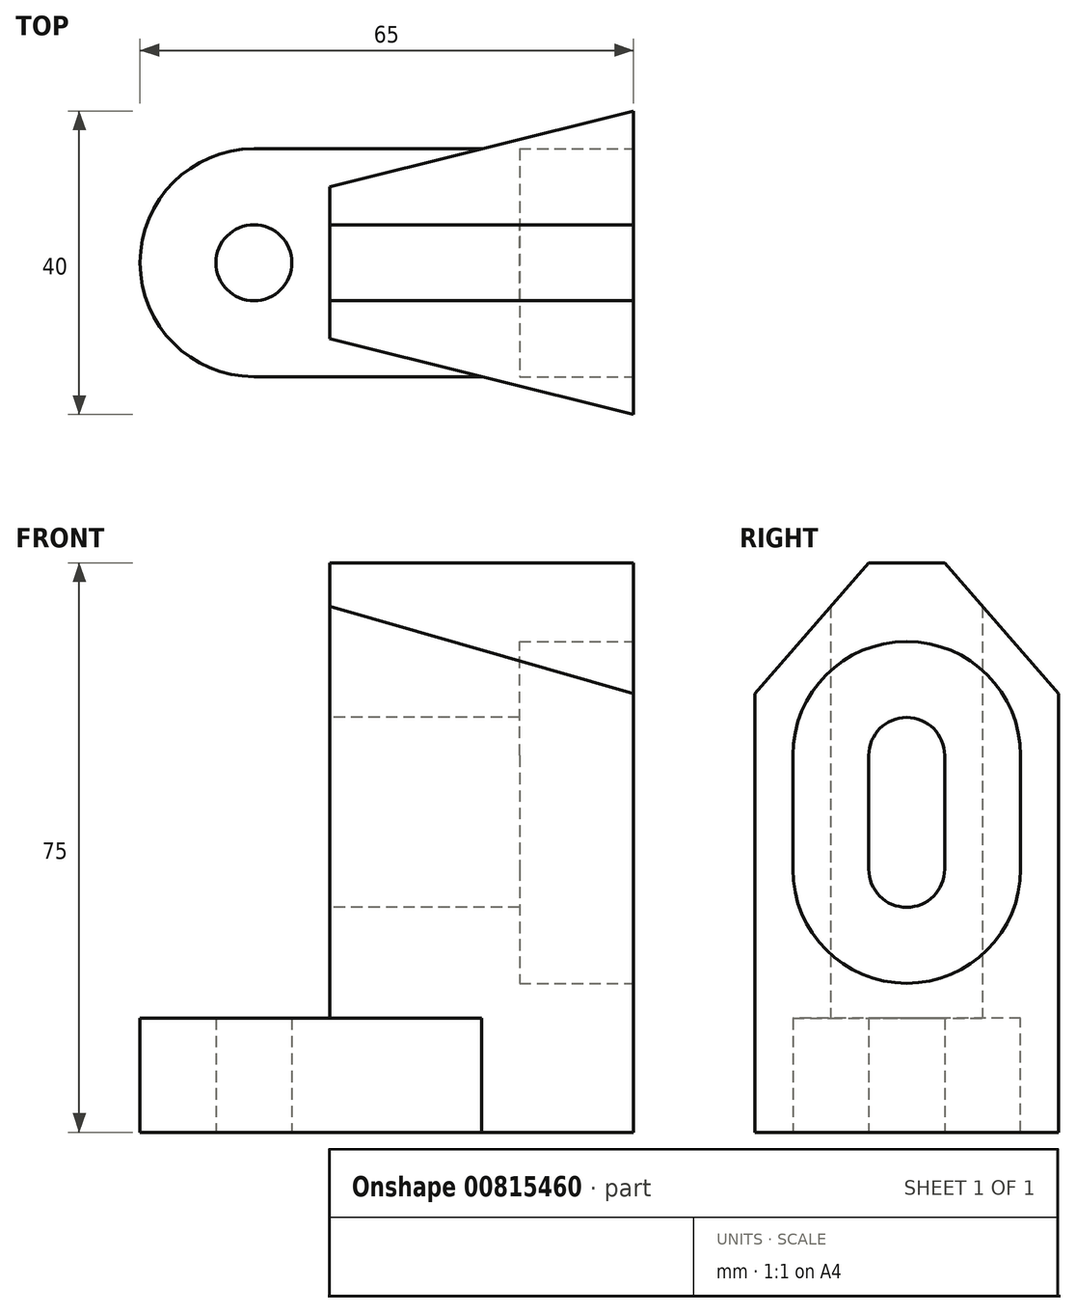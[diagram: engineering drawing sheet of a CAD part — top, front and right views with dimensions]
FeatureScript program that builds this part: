
annotation { "Feature Type Name" : "Feature", "Feature Type Description" : "" }
export const myFeature = defineFeature(function(context is Context, id is Id, definition is map)
    precondition{}
    {
        {
            var Q0;
            Q0=qCreatedBy(makeId("Top.planeOp"),FACE);
            var sketch = newSketch(context, id + "F0", { "sketchPlane" : qUnion([Q0])});
            skArc(sketch, "E0", {"start": v(-50, 15) * mm, "mid": v(-65, 0) * mm, "end": v(-50, -15) * mm});
            skLineSegment(sketch, "E1", {"start": v(-50, 15) * mm, "end": v(0, 15) * mm});
            skLineSegment(sketch, "E2", {"start": v(0, 15) * mm, "end": v(0, 0) * mm});
            skLineSegment(sketch, "E3", {"start": v(-50, -15) * mm, "end": v(0, -15) * mm});
            skLineSegment(sketch, "E4", {"start": v(0, -15) * mm, "end": v(0, 0) * mm});
            skCircle(sketch, "E5", {"center": v(-50, 0) * mm, "radius": 5 * mm});
            skSolve(sketch);
        }
        {
            var Q0;
            Q0=makeQuery(id+"F0.imprint","IMPRINT",FACE,{"disambiguationData":[TD([[makeQuery(id+"F0.imprint","IMPRINT",EDGE,{"derivedFrom":sQuery(id+"F0.wireOp",EDGE,"E0")}),1.0]])]});
            extrude(context, id + "F1", {"entities" : qUnion([Q0]), "depth" : 15 * mm, "offsetDistance" : 25 * mm});
        }
        {
            var Q0;
            Q0=makeQuery(id+"F1.opExtrude","CAP_FACE",FACE,{"disambiguationData":[OSD([sQuery(id+"F0.wireOp",EDGE,"E0"),sQuery(id+"F0.wireOp",EDGE,"E1"),sQuery(id+"F0.wireOp",EDGE,"E2"),sQuery(id+"F0.wireOp",EDGE,"E3"),sQuery(id+"F0.wireOp",EDGE,"E4"),sQuery(id+"F0.wireOp",EDGE,"E5")])],"isStart":true});
            var sketch = newSketch(context, id + "F2", { "sketchPlane" : qUnion([Q0])});
            skLineSegment(sketch, "E6", {"start": v(0, 0) * mm, "end": v(0, 20) * mm});
            skLineSegment(sketch, "E7", {"start": v(-40, 0) * mm, "end": v(-40, 10) * mm});
            skLineSegment(sketch, "E8", {"start": v(-40, 10) * mm, "end": v(0, 20) * mm});
            skLineSegment(sketch, "E9.MirrorCS", {"start": v(0, 0) * mm, "end": v(0, -20) * mm});
            skLineSegment(sketch, "E10.MirrorCS", {"start": v(-40, -10) * mm, "end": v(0, -20) * mm});
            skLineSegment(sketch, "E11.MirrorCS", {"start": v(-40, 0) * mm, "end": v(-40, -10) * mm});
            skSolve(sketch);
        }
        {
            var Q0;
            {var subQ0=sQuery(id+"F2.wireOp",EDGE,"E9.MirrorCS");var subQ1=makeQuery(id+"F1.opExtrude","CAP_EDGE",EDGE,{"disambiguationData":[OSD([sQuery(id+"F0.wireOp",EDGE,"E1")])],"isStart":true});var subQ2=makeQuery(id+"F2.imprint","INTERSECT",VERTEX,{"derivedFrom":[subQ1,subQ0]});Q0=makeQuery(id+"F2.imprint","IMPRINT",FACE,{"disambiguationData":[TD([[makeQuery(id+"F2.imprint","IMPRINT",EDGE,{"disambiguationData":[TD([[subQ2,-1.0]])],"derivedFrom":subQ0}),-1.0]])]});}
            var Q1;
            {var subQ1=sQuery(id+"F2.wireOp",EDGE,"E7");Q1=makeQuery(id+"F2.imprint","IMPRINT",FACE,{"disambiguationData":[TD([[makeQuery(id+"F2.imprint","IMPRINT",EDGE,{"derivedFrom":subQ1}),-1.0]])]});}
            var Q2;
            {var subQ0=sQuery(id+"F2.wireOp",EDGE,"E6");var subQ3=sQuery(id+"F2.wireOp",EDGE,"E8");var subQ4=makeQuery(id+"F2.imprint","INTERSECT",VERTEX,{"derivedFrom":[subQ0,subQ3]});Q2=makeQuery(id+"F2.imprint","IMPRINT",FACE,{"disambiguationData":[TD([[makeQuery(id+"F2.imprint","IMPRINT",EDGE,{"disambiguationData":[TD([[subQ4,1.0]])],"derivedFrom":subQ0}),1.0]])]});}
            extrude(context, id + "F3", {"entities" : qUnion([Q0, Q1, Q2]), "operationType" : NewBodyOperationType.ADD, "oppositeDirection" : true, "depth" : 75 * mm, "offsetDistance" : 25 * mm});
        }
        {
            var Q0;
            Q0=makeQuery(id+"F3.boolean.opBoolean","MERGE",FACE,{"derivedFrom":[makeQuery(id+"F1.opExtrude","SWEPT_FACE",FACE,{"disambiguationData":[OSD([sQuery(id+"F0.wireOp",EDGE,"E2"),sQuery(id+"F0.wireOp",EDGE,"E4")])]}),makeQuery(id+"F3.opExtrude","SWEPT_FACE",FACE,{"disambiguationData":[OSD([sQuery(id+"F2.wireOp",EDGE,"E6"),sQuery(id+"F2.wireOp",EDGE,"E9.MirrorCS")])]})]});
            var sketch = newSketch(context, id + "F4", { "sketchPlane" : qUnion([Q0])});
            skLineSegment(sketch, "E12", {"start": v(0, 75) * mm, "end": v(5, 75) * mm});
            skLineSegment(sketch, "E13", {"start": v(5, 75) * mm, "end": v(34.86, 75) * mm});
            skLineSegment(sketch, "E14", {"start": v(5, 75) * mm, "end": v(25.74, 51.14) * mm});
            skLineSegment(sketch, "E15", {"start": v(34.86, 75) * mm, "end": v(25.74, 51.14) * mm});
            skLineSegment(sketch, "E16.MirrorCS", {"start": v(0, 75) * mm, "end": v(-5, 75) * mm});
            skLineSegment(sketch, "E17.MirrorCS", {"start": v(-5, 75) * mm, "end": v(-25.74, 51.14) * mm});
            skLineSegment(sketch, "E18.MirrorCS", {"start": v(-5, 75) * mm, "end": v(-34.86, 75) * mm});
            skLineSegment(sketch, "E19.MirrorCS", {"start": v(-34.86, 75) * mm, "end": v(-25.74, 51.14) * mm});
            skSolve(sketch);
        }
        {
            var Q0;
            {var subQ3=sQuery(id+"F4.wireOp",EDGE,"E15");Q0=makeQuery(id+"F4.imprint","IMPRINT",FACE,{"disambiguationData":[TD([[makeQuery(id+"F4.imprint","IMPRINT",EDGE,{"derivedFrom":subQ3}),-1.0]])]});}
            var Q1;
            {var subQ0=sQuery(id+"F4.wireOp",EDGE,"E13");var subQ1=makeQuery(id+"F3.opExtrude","SWEPT_EDGE",EDGE,{"disambiguationData":[OSD([sQuery(id+"F2.wireOp",EDGE,"E9.MirrorCS"),sQuery(id+"F2.wireOp",EDGE,"E10.MirrorCS")])]});var subQ2=makeQuery(id+"F4.imprint","INTERSECT",VERTEX,{"derivedFrom":[subQ1,subQ0]});Q1=makeQuery(id+"F4.imprint","IMPRINT",FACE,{"disambiguationData":[TD([[makeQuery(id+"F4.imprint","IMPRINT",EDGE,{"disambiguationData":[TD([[subQ2,1.0]])],"derivedFrom":subQ0}),-1.0]])]});}
            var Q2;
            {var subQ0=sQuery(id+"F4.wireOp",EDGE,"E18.MirrorCS");var subQ1=sQuery(id+"F4.wireOp",EDGE,"E17.MirrorCS");var subQ2=makeQuery(id+"F4.imprint","INTERSECT",VERTEX,{"derivedFrom":[sQuery(id+"F4.wireOp",EDGE,"E16.MirrorCS"),subQ1,subQ0]});Q2=makeQuery(id+"F4.imprint","IMPRINT",FACE,{"disambiguationData":[TD([[makeQuery(id+"F4.imprint","IMPRINT",EDGE,{"disambiguationData":[TD([[subQ2,-1.0]])],"derivedFrom":subQ1}),-1.0]])]});}
            var Q3;
            {var subQ0=sQuery(id+"F4.wireOp",EDGE,"E19.MirrorCS");Q3=makeQuery(id+"F4.imprint","IMPRINT",FACE,{"disambiguationData":[TD([[makeQuery(id+"F4.imprint","IMPRINT",EDGE,{"derivedFrom":subQ0}),1.0]])]});}
            extrude(context, id + "F5", {"entities" : qUnion([Q0, Q1, Q2, Q3]), "operationType" : NewBodyOperationType.REMOVE, "oppositeDirection" : true, "depth" : 80 * mm, "offsetDistance" : 25 * mm});
        }
        {
            var Q0;
            Q0=makeQuery(id+"F3.opExtrude","SWEPT_FACE",FACE,{"disambiguationData":[OSD([sQuery(id+"F2.wireOp",EDGE,"E7"),sQuery(id+"F2.wireOp",EDGE,"E11.MirrorCS")])]});
            var sketch = newSketch(context, id + "F6", { "sketchPlane" : qUnion([Q0])});
            skLineSegment(sketch, "E20", {"start": v(5, 42.12) * mm, "end": v(0, 42.12) * mm});
            skArc(sketch, "E21", {"start": v(5, 49.62) * mm, "mid": v(0, 54.62) * mm, "end": v(-5, 49.62) * mm});
            skLineSegment(sketch, "E22", {"start": v(-5, 49.62) * mm, "end": v(-5, 42.12) * mm});
            skLineSegment(sketch, "E23", {"start": v(5, 49.62) * mm, "end": v(5, 42.12) * mm});
            skPoint(sketch, "E24.orphan", {"position": v(10, 42.12) * mm});
            skLineSegment(sketch, "E25.MirrorCS", {"start": v(-5, 34.62) * mm, "end": v(-5, 42.12) * mm});
            skArc(sketch, "E26.MirrorCS", {"start": v(5, 34.62) * mm, "mid": v(0, 29.62) * mm, "end": v(-5, 34.62) * mm});
            skLineSegment(sketch, "E27.MirrorCS", {"start": v(5, 34.62) * mm, "end": v(5, 42.12) * mm});
            skSolve(sketch);
        }
        {
            var Q0;
            Q0=makeQuery(id+"F6.imprint","IMPRINT",FACE,{"disambiguationData":[TD([[makeQuery(id+"F6.imprint","IMPRINT",EDGE,{"derivedFrom":sQuery(id+"F6.wireOp",EDGE,"E21")}),1.0]])]});
            extrude(context, id + "F7", {"entities" : qUnion([Q0]), "operationType" : NewBodyOperationType.REMOVE, "oppositeDirection" : true, "depth" : 50 * mm, "offsetDistance" : 25 * mm});
        }
        {
            var Q0;
            Q0=makeQuery(id+"F3.boolean.opBoolean","MERGE",FACE,{"derivedFrom":[makeQuery(id+"F1.opExtrude","SWEPT_FACE",FACE,{"disambiguationData":[OSD([sQuery(id+"F0.wireOp",EDGE,"E2"),sQuery(id+"F0.wireOp",EDGE,"E4")])]}),makeQuery(id+"F3.opExtrude","SWEPT_FACE",FACE,{"disambiguationData":[OSD([sQuery(id+"F2.wireOp",EDGE,"E6"),sQuery(id+"F2.wireOp",EDGE,"E9.MirrorCS")])]})]});
            var sketch = newSketch(context, id + "F8", { "sketchPlane" : qUnion([Q0])});
            skArc(sketch, "E28", {"start": v(15, 49.62) * mm, "mid": v(0, 64.62) * mm, "end": v(-15, 49.62) * mm});
            skArc(sketch, "E29", {"start": v(-15, 34.62) * mm, "mid": v(0, 19.62) * mm, "end": v(15, 34.62) * mm});
            skLineSegment(sketch, "E30", {"start": v(-15, 49.62) * mm, "end": v(-15, 34.62) * mm});
            skLineSegment(sketch, "E31", {"start": v(15, 49.62) * mm, "end": v(15, 34.62) * mm});
            skSolve(sketch);
        }
        {
            var Q0;
            Q0=makeQuery(id+"F8.imprint","IMPRINT",FACE,{"disambiguationData":[TD([[makeQuery(id+"F8.imprint","IMPRINT",EDGE,{"derivedFrom":sQuery(id+"F8.wireOp",EDGE,"E28")}),1.0]])]});
            extrude(context, id + "F9", {"entities" : qUnion([Q0]), "operationType" : NewBodyOperationType.REMOVE, "oppositeDirection" : true, "depth" : 15 * mm, "offsetDistance" : 25 * mm});
        }
    });
